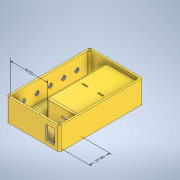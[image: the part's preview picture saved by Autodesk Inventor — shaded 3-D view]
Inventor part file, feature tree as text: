
AUTODESK INVENTOR PART (.ipt)
format: ipt  version: 2020 (Build 240168000, 168)  size: 322,560 bytes
history: native  units: mm
features: sketch x13, extrude x11, other x3, fillet x3, hole x3, projected_geometry x2
ambient origin geometry x8: Origin, YZ Plane, XZ Plane, XY Plane, X Axis, Y Axis, Z Axis, Center Point
bodies: Solid1 (feature_tree)
feature tree (35):
  other  "Annotations"
  extrude  "Extrusion1"  Depth=110.0mm
  extrude  "Extrusion2"  Depth=105.0mm
  sketch  "Sketch3"  dims[d4=30.0mm d5=0.0mm d6=3.0mm d7=0.0mm]
  extrude  "Extrusion3"  Depth=3.0mm TaperAngle=0.0deg
  extrude  "Extrusion4"  Depth=78.0mm
  extrude  "Extrusion5"  Depth=76.0mm
  fillet  "Fillet1"  Radius=25.0mm
  extrude  "Extrusion6"  Depth=2.0mm TaperAngle=0.0deg
  extrude  "Extrusion7"  Depth=3.0mm
  extrude  "Extrusion8"  Depth=3.0mm
  fillet  "Fillet2"  Radius=1.5mm
  hole  "Hole1"  [1 undecoded]
  fillet  "Fillet3"  Radius=2.0mm
  extrude  "Extrusion9"  Depth=30.0mm TaperAngle=0.0deg
  extrude  "Extrusion10"  Depth=2.0mm
  hole  "Hole3"  [1 undecoded]
  hole  "Hole4"  [1 undecoded]
  extrude  "Extrusion11"  Depth=2.0mm
  sketch  "Sketch1"  dims[d0=70.0mm d1=110.0mm]
  sketch  "Sketch2"  dims[d2=65.0mm d3=105.0mm]
  sketch  "Sketch4"  dims[d8=44.0mm d9=78.0mm]
  sketch  "Sketch5"  dims[d10=41.5mm d11=76.0mm d12=25.0mm d13=0.0mm]
  sketch  "Sketch6"  dims[d14=25.0mm d15=0.0mm d16=2.0mm d17=0.0mm]
  sketch  "Sketch7"  dims[d18=2.0mm d19=3.0mm]
  sketch  "Sketch8"  dims[d20=1.5mm d21=3.0mm d22=1.5mm]
  sketch  "Sketch9"  dims[d23=2.0mm d24=0.0mm d25=3.0mm d26=2.0mm]
  sketch  "Sketch10"  dims[d27=2.0mm d28=0.0mm d29=30.0mm d30=0.0mm]
  sketch  "Sketch12"  dims[d31=2.0mm]
  sketch  "Sketch14"  dims[d32=3.0mm d33=6.0mm d34=4.0mm d35=2.0mm d36=90.0deg d37=40.0mm d38=20.594885mm d39=2.0mm]
  sketch  "Sketch16"  dims[d40=2.0mm d41=2.0mm d42=2.0mm d43=2.0mm d44=2.0mm d45=2.0mm d46=2.0mm d47=0.0mm d48=15.0mm d49=1.5mm d50=0.0mm d58=3.75mm d59=90.0deg d60=1.0mm d61=6.0mm d62=3.5mm d63=2.0mm d64=90.0deg d65=1.0mm d66=20.594885mm d71=17.6mm d72=50.0mm d74=17.6mm d75=10.0mm d77=10.0mm d79=18.0mm d80=5.5mm d81=6.0mm d82=3.5mm d83=2.0mm d84=90.0deg d85=3.0mm d86=0.0mm d88=4.0mm d89=180.0deg d90=12.0mm d91=19.0mm d92=3.0mm d93=0.0mm d69=6.515894mm d70=27.0mm d94=15.238305mm d95=9.122444mm d96=49.5mm]
  projected_geometry  "Project Cut Edges1"
  projected_geometry  "Project Cut Edges2"
  other  "Linear Dimension 1"
  other  "Linear Dimension 2"
note: 3 required parameter values undecoded (feature->parameter linkage not recoverable at this tier; creation-order binding heuristic only, values carry confidence <= 0.55)
